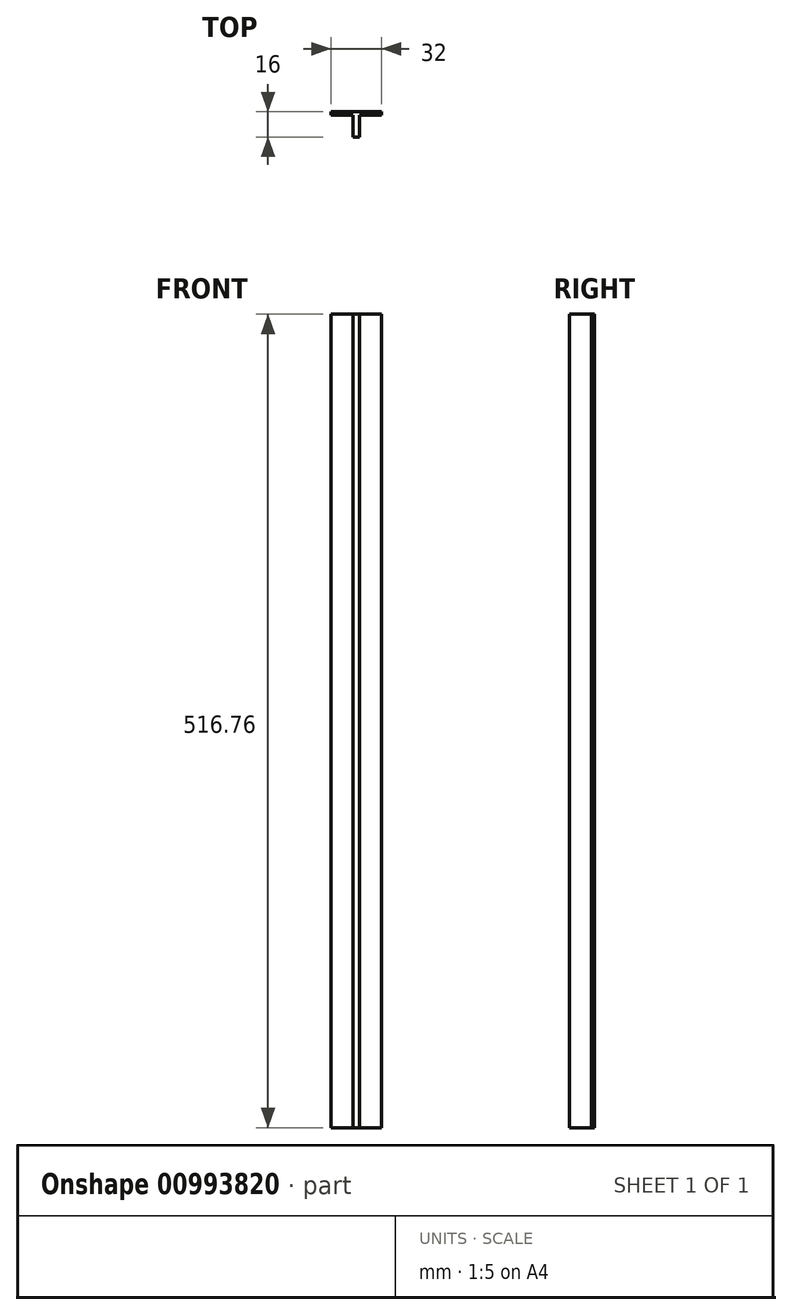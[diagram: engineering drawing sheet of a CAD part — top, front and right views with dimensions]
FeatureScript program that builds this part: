
annotation { "Feature Type Name" : "Feature", "Feature Type Description" : "" }
export const myFeature = defineFeature(function(context is Context, id is Id, definition is map)
    precondition{}
    {
        {
            var Q0;
            Q0=qCreatedBy(makeId("Top.planeOp"),FACE);
            var sketch = newSketch(context, id + "F0", { "sketchPlane" : qUnion([Q0])});
            skLineSegment(sketch, "E0.bottom", {"start": v(16, 1) * mm, "end": v(-16, 1) * mm});
            skLineSegment(sketch, "E0.top", {"start": v(16, -1) * mm, "end": v(2, -1) * mm});
            skLineSegment(sketch, "E0.left", {"start": v(16, 1) * mm, "end": v(16, -1) * mm});
            skLineSegment(sketch, "E0.right", {"start": v(-16, 1) * mm, "end": v(-16, -1) * mm});
            skPoint(sketch, "E0.middle", {"position": v(0, 0) * mm});
            skLineSegment(sketch, "E1.top", {"start": v(-2, -15) * mm, "end": v(2, -15) * mm});
            skLineSegment(sketch, "E1.left", {"start": v(-2, -1) * mm, "end": v(-2, -15) * mm});
            skLineSegment(sketch, "E1.right", {"start": v(2, -1) * mm, "end": v(2, -15) * mm});
            skLineSegment(sketch, "E2.trimOffspring", {"start": v(-2, -1) * mm, "end": v(-16, -1) * mm});
            skSolve(sketch);
        }
        {
            var Q0;
            Q0=makeQuery(id+"F0.imprint","IMPRINT",FACE,{"disambiguationData":[TD([[makeQuery(id+"F0.imprint","IMPRINT",EDGE,{"derivedFrom":sQuery(id+"F0.wireOp",EDGE,"E0.bottom")}),1.0]])]});
            extrude(context, id + "F1", {"entities" : qUnion([Q0]), "depth" : 516.77 * mm, "offsetDistance" : 25 * mm, "symmetric" : true});
        }
    });
